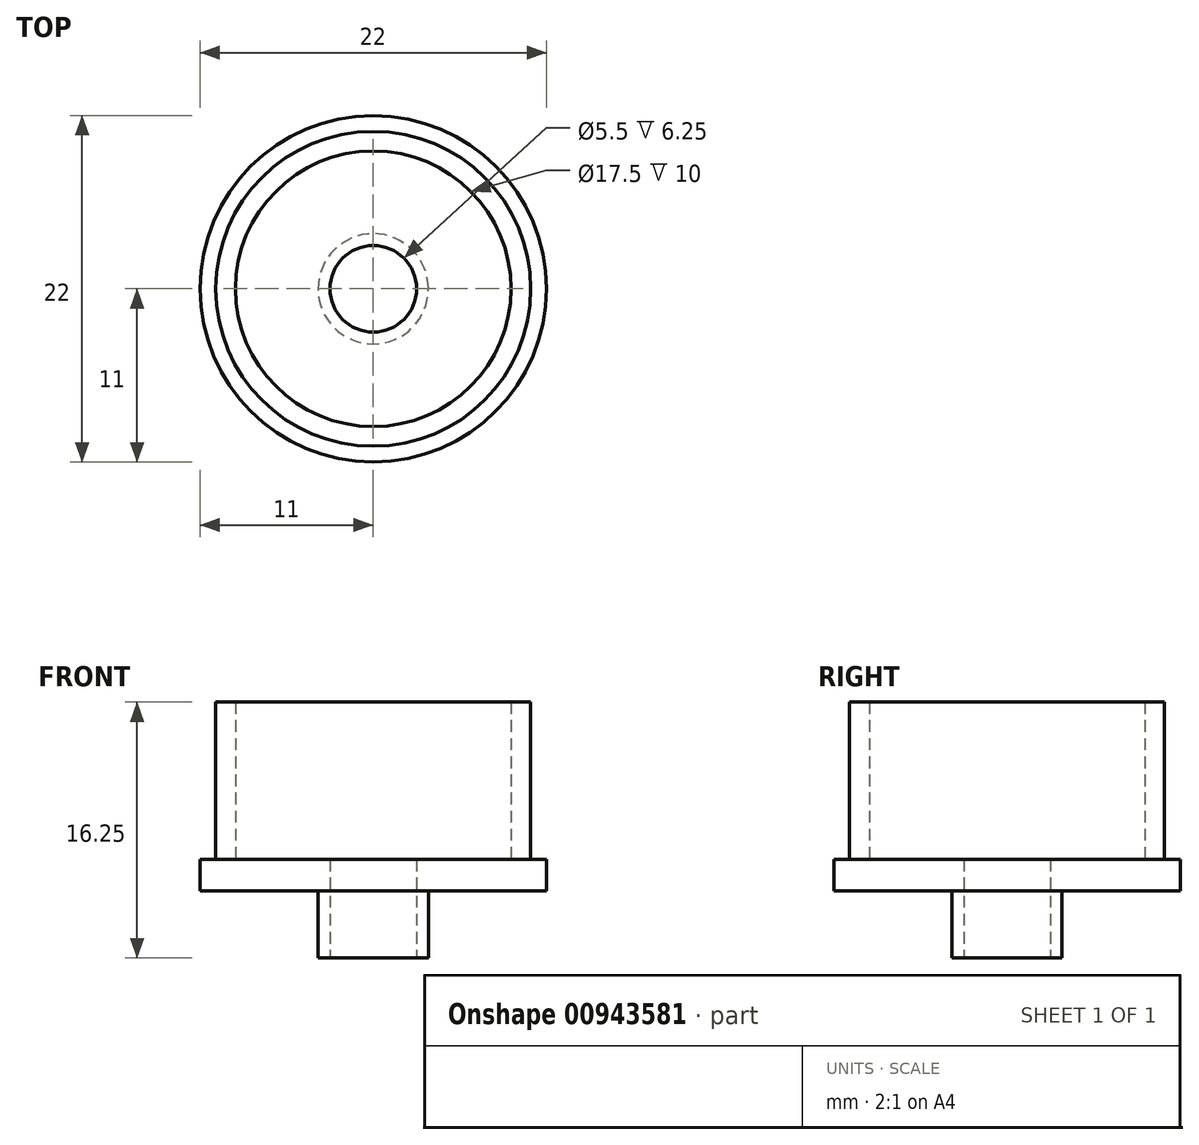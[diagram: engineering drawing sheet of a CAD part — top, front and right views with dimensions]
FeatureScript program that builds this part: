
annotation { "Feature Type Name" : "Feature", "Feature Type Description" : "" }
export const myFeature = defineFeature(function(context is Context, id is Id, definition is map)
    precondition{}
    {
        {
            var Q0;
            Q0=qCreatedBy(makeId("Top.planeOp"),FACE);
            var sketch = newSketch(context, id + "F0", { "sketchPlane" : qUnion([Q0])});
            skCircle(sketch, "E0", {"center": v(0, 0) * mm, "radius": 11 * mm});
            skCircle(sketch, "E1", {"center": v(0, 0) * mm, "radius": 10 * mm});
            skCircle(sketch, "E2", {"center": v(0, 0) * mm, "radius": 3.5 * mm});
            skCircle(sketch, "E3", {"center": v(0, 0) * mm, "radius": 8.75 * mm});
            skCircle(sketch, "E4", {"center": v(0, 0) * mm, "radius": 7.25 * mm});
            skCircle(sketch, "E5", {"center": v(0, 0) * mm, "radius": 2.75 * mm});
            skSolve(sketch);
        }
        {
            var Q0;
            Q0 = qSketchRegion(id + "F0", true);
            var Q1;
            Q1=makeQuery(id+"F0.imprint","IMPRINT",FACE,{"disambiguationData":[TD([[makeQuery(id+"F0.imprint","IMPRINT",EDGE,{"derivedFrom":sQuery(id+"F0.wireOp",EDGE,"E1")}),1.0]])]});
            var Q2;
            Q2=makeQuery(id+"F0.imprint","IMPRINT",FACE,{"disambiguationData":[TD([[makeQuery(id+"F0.imprint","IMPRINT",EDGE,{"derivedFrom":sQuery(id+"F0.wireOp",EDGE,"E3")}),1.0]])]});
            var Q3;
            Q3=makeQuery(id+"F0.imprint","IMPRINT",FACE,{"disambiguationData":[TD([[makeQuery(id+"F0.imprint","IMPRINT",EDGE,{"derivedFrom":sQuery(id+"F0.wireOp",EDGE,"E2")}),-1.0]])]});
            var Q4;
            Q4=makeQuery(id+"F0.imprint","IMPRINT",FACE,{"disambiguationData":[TD([[makeQuery(id+"F0.imprint","IMPRINT",EDGE,{"derivedFrom":sQuery(id+"F0.wireOp",EDGE,"E2")}),1.0]])]});
            extrude(context, id + "F1", {"entities" : qUnion([Q0, Q1, Q2, Q3, Q4]), "depth" : 2 * mm, "offsetDistance" : 25 * mm});
        }
        {
            var Q0;
            Q0=makeQuery(id+"F0.imprint","IMPRINT",FACE,{"disambiguationData":[TD([[makeQuery(id+"F0.imprint","IMPRINT",EDGE,{"derivedFrom":sQuery(id+"F0.wireOp",EDGE,"E2")}),1.0]])]});
            extrude(context, id + "F2", {"entities" : qUnion([Q0]), "operationType" : NewBodyOperationType.ADD, "oppositeDirection" : true, "depth" : 4.25 * mm, "offsetDistance" : 25 * mm});
        }
        {
            var Q0;
            Q0=makeQuery(id+"F0.imprint","IMPRINT",FACE,{"disambiguationData":[TD([[makeQuery(id+"F0.imprint","IMPRINT",EDGE,{"derivedFrom":sQuery(id+"F0.wireOp",EDGE,"E1")}),1.0]])]});
            extrude(context, id + "F3", {"entities" : qUnion([Q0]), "operationType" : NewBodyOperationType.ADD, "depth" : 12 * mm, "offsetDistance" : 25 * mm});
        }
    });
